# Revit family: Haworth_HATElements_BenchSingle_AP_PRELIMINARY
name_source: partatom
category: Furniture
units: mm (PartAtom-declared; Revit-internal decimal feet)

## family parameters
Always vertical = Yes
Cut with Voids When Loaded = No
OmniClass Number = 23.40.70.14.64.11
OmniClass Title = Office Furniture
Room Calculation Point = No
Shared = No
Work Plane-Based = No

## types (6) — shared parameters
Actual Height = 730 mm  [stored 2.39501 ft]
Assembly Code = E2020200
Base Tube Finish = Haworth _ Paint _ Smoke
Box Body Finish = Haworth _ Paint _ Black
Cable Tray Finish = Haworth _ Polymer _ Undecided
Cable Tray Width = 600 mm
Description = Haworth - HAT Elements - Single Bench
Flip Top Finish = Haworth _ Paint _ Metallic Silver
Leg Height = 695 mm  [stored 2.28018 ft]
Manufacturer = Haworth
Model = SYELSBXXXX
Revision Number = 1
Size = Verify Final Dim.w/ Haworth
Trim Finish = Haworth _ Metal _ Structured White EC
URL = https://www.haworth.com
URL - Product = https://www.haworth.com
Warranty = http://www.haworth.com
Worksurface Depth = 600, 700, 750, 800 mm
Worksurface Width = 1200, 1400, 1500, 1600, 1800 mm
with Worktop = Yes
without Height Adjustment = Yes

## per-type parameters (varying)
| type | Actual Depth | Actual Width | Cable Tray | Flip Top Cable Outlet | Handcrank | Leg Connector for Trunk | Rectangular Motorized | Round Leg | Round Motorized | Square Leg | Square Motorized | Umbilical Cord to Floor | Umbilical Cord to Trunk | Understructure Width | with Height Adjustment |
| 1800 x 800 | 800 mm  [stored 2.62467 ft] | 1800 mm  [stored 5.90551 ft] | Yes | Yes | No | Yes | No | No | No | Yes | Yes | Yes | No | 1680 mm  [stored 5.51181 ft] | Yes |
| 1200 x 600 | 600 mm | 1200 mm | Yes | Yes | No | Yes | No | Yes | Yes | No | No | Yes | No | 1080 mm | Yes |
| 1500 x 700 | 700 mm  [stored 2.29659 ft] | 1500 mm  [stored 4.92126 ft] | Yes | Yes | No | No | Yes | No | No | Yes | No | No | No | 1380 mm  [stored 4.52756 ft] | Yes |
| 1000 x 750 | 750 mm  [stored 2.46063 ft] | 1000 mm  [stored 3.28084 ft] | No | No | No | No | No | No | No | Yes | No | No | No | 880 mm | No |
| 1600 x 750 | 750 mm  [stored 2.46063 ft] | 1600 mm | Yes | Yes | No | Yes | Yes | No | No | Yes | No | Yes | No | 1480 mm | Yes |
| 1400 x 800 | 800 mm  [stored 2.62467 ft] | 1400 mm | No | Yes | Yes | Yes | No | No | No | Yes | No | No | Yes | 1280 mm | Yes |

note: [stored X ft] marks values corroborated as IEEE doubles in the binary element streams (Revit-internal decimal feet)

## geometry (parser evidence)
native form markers: Sweep x41
no freeform markers — native parametric forms only
